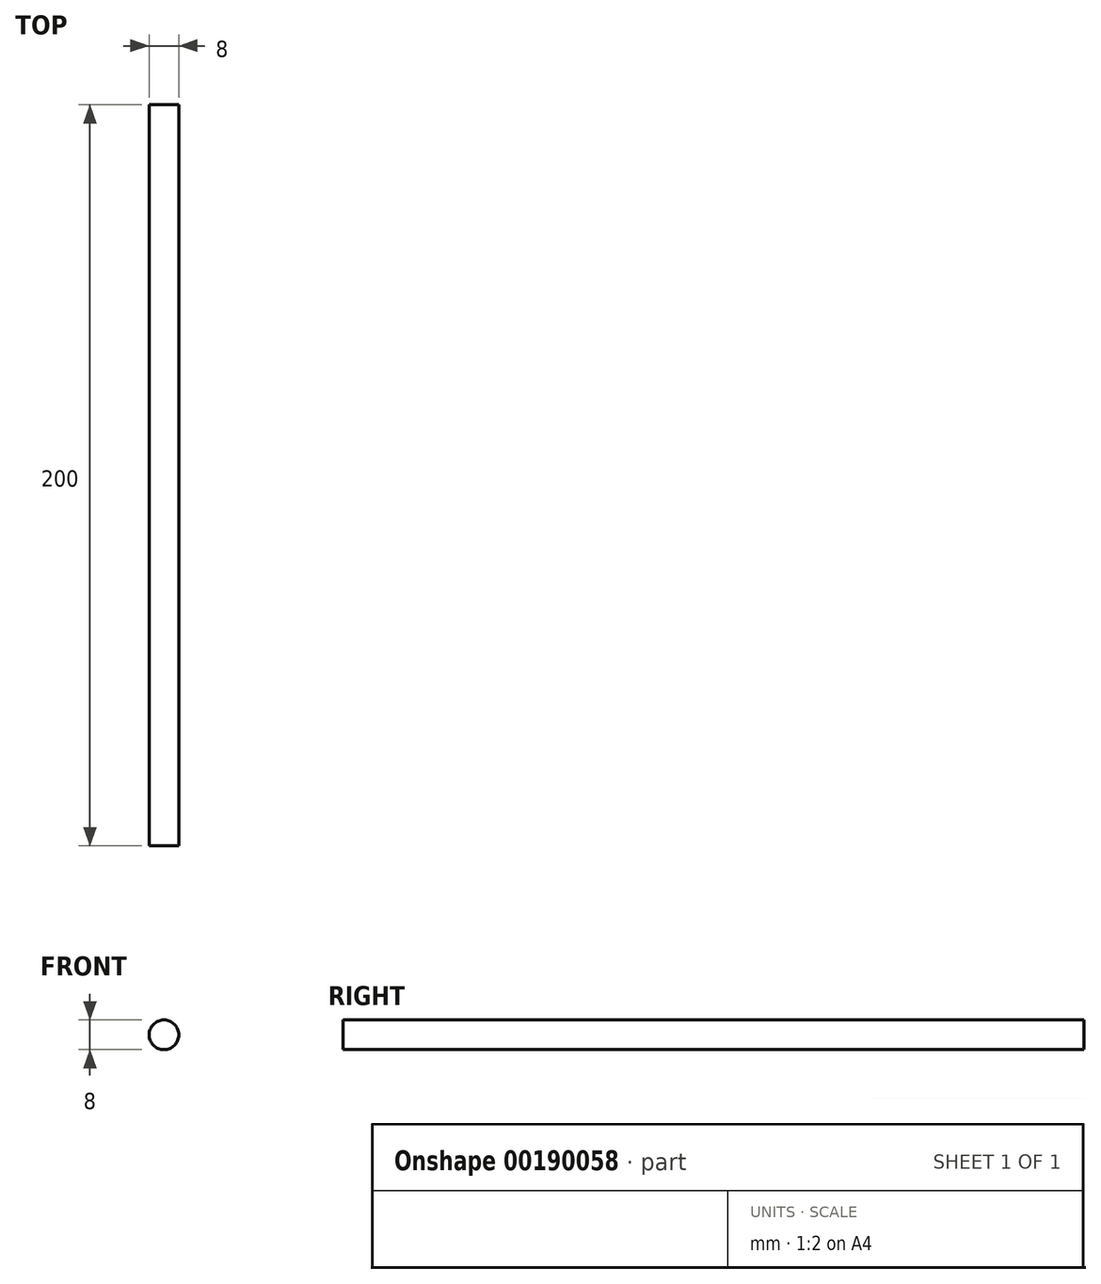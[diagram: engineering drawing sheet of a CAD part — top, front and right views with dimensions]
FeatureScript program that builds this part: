
annotation { "Feature Type Name" : "Feature", "Feature Type Description" : "" }
export const myFeature = defineFeature(function(context is Context, id is Id, definition is map)
    precondition{}
    {
        {
            var Q0;
            Q0=qCreatedBy(makeId("Front.planeOp"),FACE);
            var sketch = newSketch(context, id + "F0", { "sketchPlane" : qUnion([Q0])});
            skCircle(sketch, "E0", {"center": v(0, 0) * mm, "radius": 4 * mm});
            skSolve(sketch);
        }
        {
            var Q0;
            Q0=qSketchRegion(id+"F0",true);
            extrude(context, id + "F1", {"entities" : qUnion([Q0]), "depth" : 200 * mm});
        }
    });
